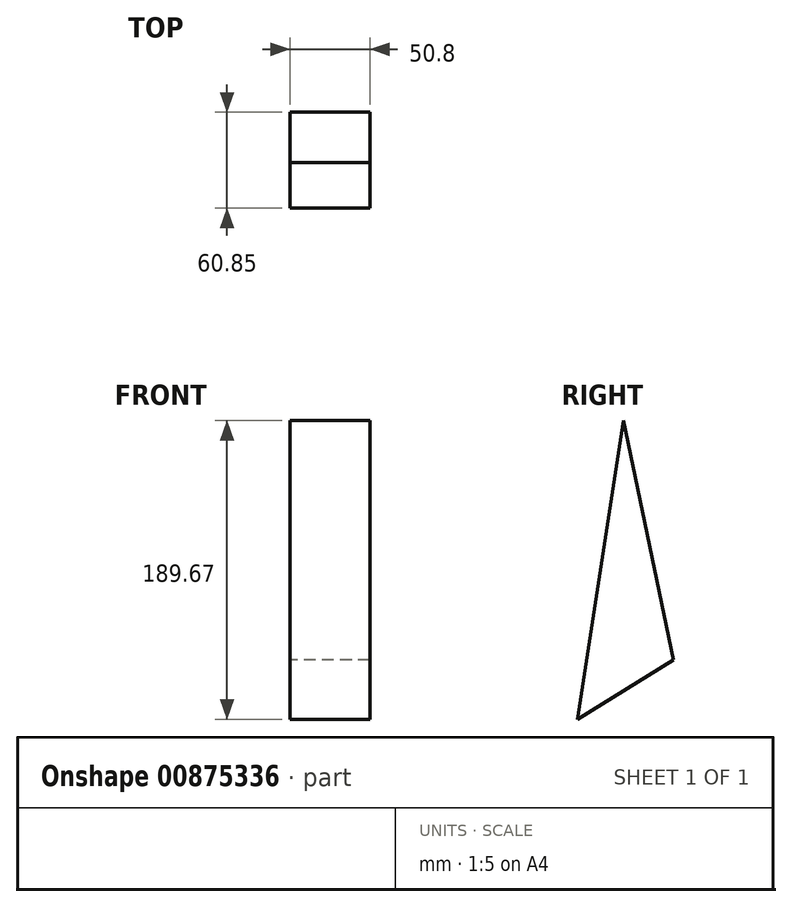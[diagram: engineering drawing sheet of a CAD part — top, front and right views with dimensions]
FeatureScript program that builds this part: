
annotation { "Feature Type Name" : "Feature", "Feature Type Description" : "" }
export const myFeature = defineFeature(function(context is Context, id is Id, definition is map)
    precondition{}
    {
        {
            var Q0;
            Q0=qCreatedBy(makeId("Right.planeOp"),FACE);
            var sketch = newSketch(context, id + "F0", { "sketchPlane" : qUnion([Q0])});
            skPoint(sketch, "E0", {"position": v(99.95, 77.37) * mm});
            skLineSegment(sketch, "E1", {"start": v(27.17, -57.19) * mm, "end": v(131.7, -74.55) * mm});
            skLineSegment(sketch, "E2", {"start": v(-26.9, -92.37) * mm, "end": v(70.86, -112.3) * mm});
            skLineSegment(sketch, "E3", {"start": v(70.86, -112.3) * mm, "end": v(99.95, 77.37) * mm});
            skLineSegment(sketch, "E4", {"start": v(99.95, 77.37) * mm, "end": v(131.7, -74.55) * mm});
            skLineSegment(sketch, "E5", {"start": v(70.86, -112.3) * mm, "end": v(131.7, -74.55) * mm});
            skLineSegment(sketch, "E6", {"start": v(0, 77.37) * mm, "end": v(99.95, 77.37) * mm});
            skSolve(sketch);
        }
        {
            var Q0;
            Q0 = qSketchRegion(id + "F0", true);
            var Q1;
            Q1 = qSketchRegion(id + "Fw4Kb9CX4iXRKhF_0", true);
            extrude(context, id + "F1", {"entities" : qUnion([Q0, Q1]), "depth" : 50.8 * mm, "offsetDistance" : 25.4 * mm});
        }
    });
